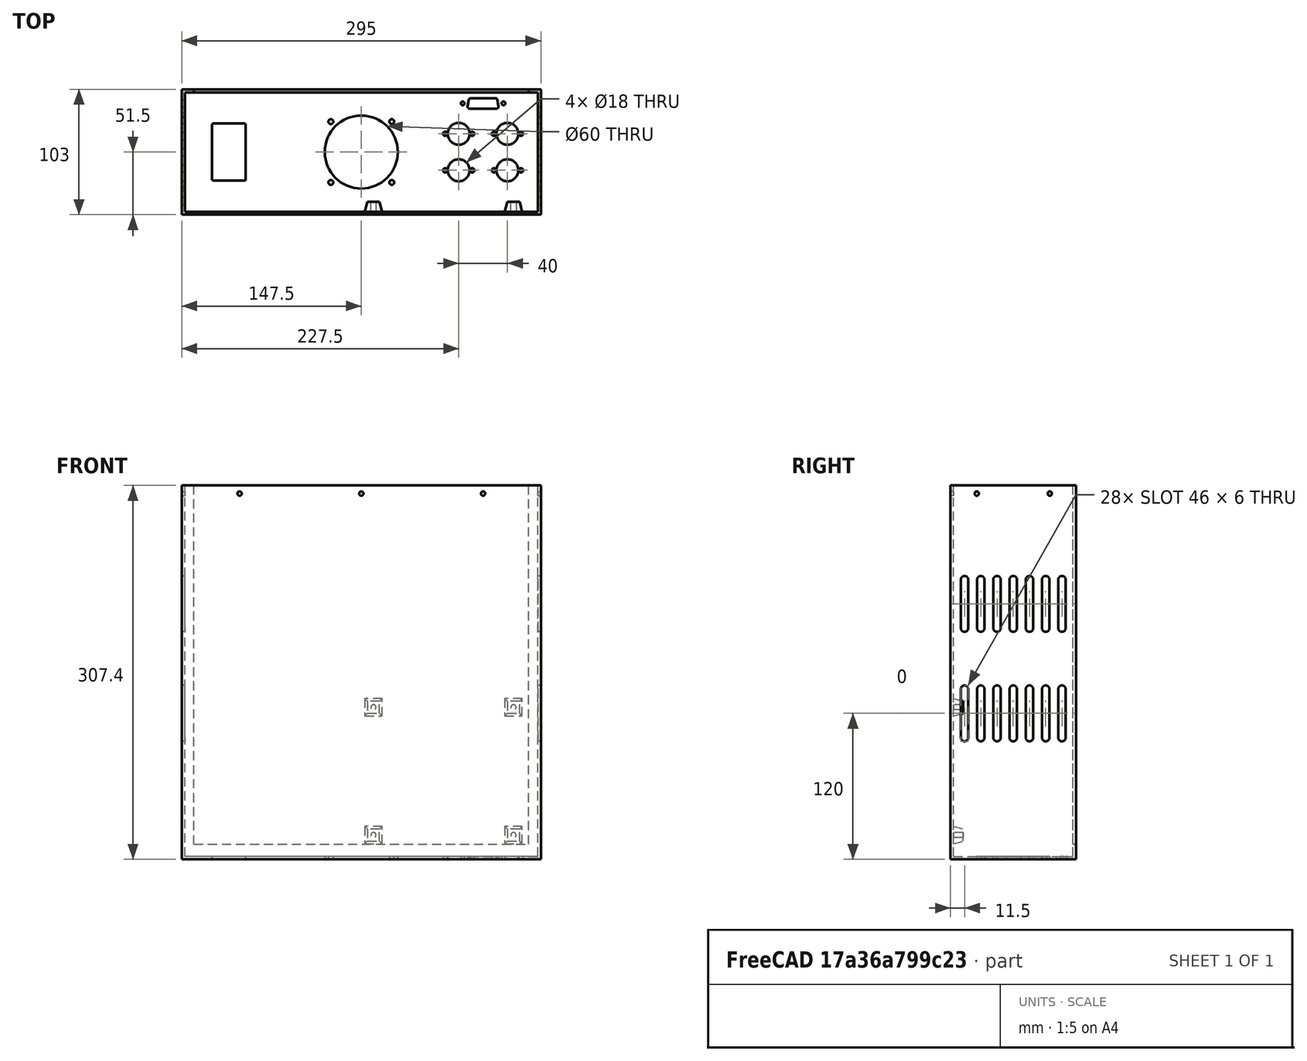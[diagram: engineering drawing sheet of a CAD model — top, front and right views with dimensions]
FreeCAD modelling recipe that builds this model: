
FCSTD DOCUMENT  (FreeCAD 1.0R39109 (Git))
Label: Main case
License: All rights reserved
LicenseURL: http://en.wikipedia.org/wiki/All_rights_reserved
objects: Sketcher::SketchObject×10, TechDraw::DrawViewDimension×7, PartDesign::Pocket×6, PartDesign::LinearPattern×6, PartDesign::Pad×4, PartDesign::MultiTransform×3, TechDraw::DrawSVGTemplate×2, TechDraw::DrawViewBalloon×2, TechDraw::DrawPage×2, PartDesign::Draft×1, PartDesign::Body×1, TechDraw::DrawProjGroupItem×1, TechDraw::DrawProjGroup×1, Mesh::Feature×1
note: 82 computed .brp shape members not serialized (recipe doc carries the construction recipe); baked Part::Feature solids carry a one-line shape summary decoded from their .brp

FEATURE [Sketcher::SketchObject] Sketch
  ArcFitTolerance = 0
  AttachmentSupport = -> [XY_Plane]
  FullyConstrained = true
  MakeInternals = false
  MapMode = 5
  sketch-geometry (4):
    g0: LineSegment StartX=-147.5 StartY=51.5 StartZ=0 EndX=147.5 EndY=51.5 EndZ=0
    g1: LineSegment StartX=147.5 StartY=51.5 StartZ=0 EndX=147.5 EndY=-51.5 EndZ=0
    g2: LineSegment StartX=147.5 StartY=-51.5 StartZ=0 EndX=-147.5 EndY=-51.5 EndZ=0
    g3: LineSegment StartX=-147.5 StartY=-51.5 StartZ=0 EndX=-147.5 EndY=51.5 EndZ=0
  constraints (11):
    c: Coincident(g0,g1)
    c: Coincident(g1,g2)
    c: Coincident(g2,g3)
    c: Coincident(g3,g0)
    c: Horizontal(g0)
    c: Horizontal(g2)
    c: Vertical(g1)
    c: Vertical(g3)
    c: Symmetric(g0,g1,g-1)
    c: DistanceX(g0,g0) = 295
    c: DistanceY(g1,g1) = 103
FEATURE [PartDesign::Pad] Pad  label="Rear panel"
  Direction = (0,0,1)
  Length = 2.4
  Length2 = 10
  Profile = -> Sketch
  ReferenceAxis = -> Sketch [N_Axis]
  Suppressed = false
  Type = 0
FEATURE [Sketcher::SketchObject] Sketch001
  ArcFitTolerance = 0
  AttachmentSupport = -> [Pad]
  FullyConstrained = true
  MakeInternals = false
  MapMode = 5
  Placement = pos=(0,0,2.4) rot=(0,0,1;0rad)
  sketch-geometry (14):
    g0: LineSegment [constr] StartX=-147.5 StartY=51.5 StartZ=0 EndX=147.5 EndY=51.5 EndZ=0
    g1: LineSegment StartX=147.5 StartY=51.5 StartZ=0 EndX=147.5 EndY=-51.5 EndZ=0
    g2: LineSegment StartX=147.5 StartY=-51.5 StartZ=0 EndX=-147.5 EndY=-51.5 EndZ=0
    g3: LineSegment StartX=-147.5 StartY=-51.5 StartZ=0 EndX=-147.5 EndY=51.5 EndZ=0
    g4: LineSegment [constr] StartX=-145 StartY=49 StartZ=0 EndX=145 EndY=49 EndZ=0
    g5: LineSegment StartX=145 StartY=49 StartZ=0 EndX=145 EndY=-49 EndZ=0
    g6: LineSegment StartX=145 StartY=-49 StartZ=0 EndX=-145 EndY=-49 EndZ=0
    g7: LineSegment StartX=-145 StartY=-49 StartZ=0 EndX=-145 EndY=49 EndZ=0
    g8: LineSegment StartX=-147.5 StartY=51.5 StartZ=0 EndX=-137.5 EndY=51.5 EndZ=0
    g9: LineSegment StartX=-137.5 StartY=51.5 StartZ=0 EndX=-137.5 EndY=49 EndZ=0
    g10: LineSegment StartX=-137.5 StartY=49 StartZ=0 EndX=-145 EndY=49 EndZ=0
    g11: LineSegment StartX=147.5 StartY=51.5 StartZ=0 EndX=137.5 EndY=51.5 EndZ=0
    g12: LineSegment StartX=137.5 StartY=51.5 StartZ=0 EndX=137.5 EndY=49 EndZ=0
    g13: LineSegment StartX=137.5 StartY=49 StartZ=0 EndX=145 EndY=49 EndZ=0
  constraints (38):
    c: Coincident(g0,g1)
    c: Coincident(g1,g2)
    c: Coincident(g2,g3)
    c: Coincident(g3,g0)
    c: Horizontal(g0)
    c: Horizontal(g2)
    c: Vertical(g1)
    c: Vertical(g3)
    c: Symmetric(g1,g0,g-1)
    c: DistanceX(g0,g0) = 295
    c: DistanceY(g3,g3) = 103
    c: Coincident(g4,g5)
    c: Coincident(g5,g6)
    c: Coincident(g6,g7)
    c: Coincident(g7,g4)
    c: Horizontal(g4)
    c: Horizontal(g6)
    c: Vertical(g5)
    c: Vertical(g7)
    c: Symmetric(g4,g5,g-1)
    c: DistanceX(g4,g4) = 290
    c: DistanceY(g7,g7) = 98
    c: Coincident(g3,g8)
    c: PointOnObject(g8,g0)
    c: Coincident(g8,g9)
    c: PointOnObject(g9,g4)
    c: Vertical(g9)
    c: Coincident(g9,g10)
    c: Coincident(g10,g7)
    c: DistanceX(g8,g8) = 10
    c: Coincident(g1,g11)
    c: PointOnObject(g11,g0)
    c: Coincident(g11,g12)
    c: PointOnObject(g12,g4)
    c: Coincident(g12,g13)
    c: Coincident(g13,g5)
    c: Vertical(g12)
    c: DistanceX(g11,g11) = 10
FEATURE [PartDesign::Pad] Pad001  label="Bottom and sides"
  BaseFeature = -> Pad
  Direction = (0,0,1)
  Length = 305
  Length2 = 10
  Profile = -> Sketch001
  ReferenceAxis = -> Sketch001 [N_Axis]
  Suppressed = false
  Type = 0
FEATURE [Sketcher::SketchObject] Sketch002
  ArcFitTolerance = 0
  AttachmentSupport = -> [Pad001]
  FullyConstrained = true
  MakeInternals = false
  MapMode = 5
  Placement = pos=(0,0,2.4) rot=(0,0,1;0rad)
  sketch-geometry (4):
    g0: LineSegment StartX=-137.5 StartY=51.5 StartZ=0 EndX=137.5 EndY=51.5 EndZ=0
    g1: LineSegment StartX=137.5 StartY=51.5 StartZ=0 EndX=137.5 EndY=49 EndZ=0
    g2: LineSegment StartX=137.5 StartY=49 StartZ=0 EndX=-137.5 EndY=49 EndZ=0
    g3: LineSegment StartX=-137.5 StartY=49 StartZ=0 EndX=-137.5 EndY=51.5 EndZ=0
  constraints (11):
    c: Coincident(g0,g1)
    c: Coincident(g1,g2)
    c: Coincident(g2,g3)
    c: Coincident(g3,g0)
    c: Horizontal(g0)
    c: Vertical(g1)
    c: Vertical(g3)
    c: DistanceX(g0,g0) = 275
    c: DistanceY(g-1,g0) = 51.5
    c: DistanceY(g3,g3) = 2.5
    c: Symmetric(g1,g2,g-2)
FEATURE [PartDesign::Pad] Pad002  label="Rear top return"
  BaseFeature = -> Pad001
  Direction = (0,0,1)
  Length = 10
  Length2 = 10
  Profile = -> Sketch002
  ReferenceAxis = -> Sketch002 [N_Axis]
  Suppressed = false
  Type = 0
FEATURE [Sketcher::SketchObject] Sketch003
  ArcFitTolerance = 0
  AttachmentSupport = -> [Pad002]
  FullyConstrained = true
  MakeInternals = false
  MapMode = 5
  Placement = pos=(-147.5,0,0) rot=(0.57735,-0.57735,-0.57735;2.0944rad)
  sketch-geometry (4):
    g0: ArcOfCircle CenterX=40 CenterY=140 CenterZ=0 NormalX=0 NormalY=0 NormalZ=1 AngleXU=0 Radius=3 StartAngle=-2.7e-15 EndAngle=3.14159
    g1: ArcOfCircle CenterX=40 CenterY=100 CenterZ=0 NormalX=0 NormalY=0 NormalZ=1 AngleXU=0 Radius=3 StartAngle=3.14159 EndAngle=6.28319
    g2: LineSegment StartX=37 StartY=140 StartZ=0 EndX=37 EndY=100 EndZ=0
    g3: LineSegment StartX=43 StartY=100 StartZ=0 EndX=43 EndY=140 EndZ=0
  constraints (10):
    c: Tangent(g0,g2) = -1.5708
    c: Tangent(g2,g1) = -1.5708
    c: Tangent(g1,g3) = -1.5708
    c: Tangent(g3,g0) = -1.5708
    c: Equal(g0,g1)
    c: Vertical(g2)
    c: Diameter(g1) = 6
    c: DistanceY(g1,g0) = 40
    c: DistanceY(g-1,g1) = 100
    c: DistanceX(g-1,g1) = 40
FEATURE [PartDesign::Pocket] Pocket  label="Vent hole"
  BaseFeature = -> Pad002
  Direction = (1,0,0)
  Length = 5
  Length2 = 5
  Profile = -> Sketch003
  ReferenceAxis = -> Sketch003 [N_Axis]
  Suppressed = false
  Type = 1
FEATURE [PartDesign::LinearPattern] LinearPattern
  Direction = -> Sketch003 [V_Axis]
  Length = 90
  Mode = 0
  Occurrences = 2
  Offset = 90
  Suppressed = false
  TransformMode = 0
FEATURE [PartDesign::LinearPattern] LinearPattern001
  Direction = -> Sketch003 [H_Axis]
  Length = 80
  Mode = 0
  Occurrences = 7
  Offset = 13.3333
  Reversed = true
  Suppressed = false
  TransformMode = 0
FEATURE [PartDesign::MultiTransform] MultiTransform  label="Vent hole array"
  BaseFeature = -> Pocket
  Originals = -> [Pocket]
  Suppressed = false
  TransformMode = 0
  Transformations = -> [LinearPattern,LinearPattern001]
FEATURE [Sketcher::SketchObject] Sketch004
  ArcFitTolerance = 0
  AttachmentSupport = -> [MultiTransform]
  FullyConstrained = true
  MakeInternals = false
  MapMode = 5
  Placement = pos=(0,0,0) rot=(1,0,0;3.14159rad)
  sketch-geometry (19):
    g0: ArcOfCircle CenterX=-121.5 CenterY=22.5 CenterZ=0 NormalX=0 NormalY=0 NormalZ=1 AngleXU=0 Radius=1 StartAngle=1.5708 EndAngle=3.14159
    g1: LineSegment StartX=-121.5 StartY=23.5 StartZ=0 EndX=-96 EndY=23.5 EndZ=0
    g2: ArcOfCircle CenterX=-96 CenterY=22.5 CenterZ=0 NormalX=0 NormalY=0 NormalZ=1 AngleXU=0 Radius=1 StartAngle=8e-16 EndAngle=1.5708
    g3: LineSegment StartX=-95 StartY=22.5 StartZ=0 EndX=-95 EndY=-22.5 EndZ=0
    g4: ArcOfCircle CenterX=-96 CenterY=-22.5 CenterZ=0 NormalX=0 NormalY=0 NormalZ=1 AngleXU=0 Radius=1 StartAngle=4.71239 EndAngle=6.28319
    g5: LineSegment StartX=-96 StartY=-23.5 StartZ=0 EndX=-121.5 EndY=-23.5 EndZ=0
    g6: ArcOfCircle CenterX=-121.5 CenterY=-22.5 CenterZ=0 NormalX=0 NormalY=0 NormalZ=1 AngleXU=0 Radius=1 StartAngle=3.14159 EndAngle=4.71239
    g7: LineSegment StartX=-122.5 StartY=-22.5 StartZ=0 EndX=-122.5 EndY=22.5 EndZ=0
    g8: GeomPoint [constr] X=-122.5 Y=23.5 Z=0
    g9: GeomPoint [constr] X=-95 Y=-23.5 Z=0
    g10: Circle CenterX=0 CenterY=0 CenterZ=0 NormalX=0 NormalY=0 NormalZ=1 AngleXU=0 Radius=30
    g11: Circle CenterX=-25 CenterY=25 CenterZ=0 NormalX=0 NormalY=0 NormalZ=1 AngleXU=0 Radius=2
    g12: Circle CenterX=25 CenterY=25 CenterZ=0 NormalX=0 NormalY=0 NormalZ=1 AngleXU=0 Radius=2
    g13: Circle CenterX=-25 CenterY=-25 CenterZ=0 NormalX=0 NormalY=0 NormalZ=1 AngleXU=0 Radius=2
    g14: Circle CenterX=25 CenterY=-25 CenterZ=0 NormalX=0 NormalY=0 NormalZ=1 AngleXU=0 Radius=2
    g15: LineSegment [constr] StartX=-25 StartY=25 StartZ=0 EndX=25 EndY=25 EndZ=0
    g16: LineSegment [constr] StartX=25 StartY=25 StartZ=0 EndX=25 EndY=-25 EndZ=0
    g17: LineSegment [constr] StartX=25 StartY=-25 StartZ=0 EndX=-25 EndY=-25 EndZ=0
    g18: LineSegment [constr] StartX=-25 StartY=-25 StartZ=0 EndX=-25 EndY=25 EndZ=0
  constraints (44):
    c: Tangent(g0,g1) = 1.5708
    c: Tangent(g1,g2) = 1.5708
    c: Tangent(g2,g3) = 1.5708
    c: Tangent(g3,g4) = 1.5708
    c: Tangent(g4,g5) = 1.5708
    c: Tangent(g5,g6) = 1.5708
    c: Tangent(g6,g7) = 1.5708
    c: Tangent(g7,g0) = 1.5708
    c: Horizontal(g1)
    c: Horizontal(g5)
    c: Vertical(g3)
    c: Vertical(g7)
    c: Equal(g0,g2)
    c: Equal(g4,g6)
    c: PointOnObject(g8,g1)
    c: PointOnObject(g8,g7)
    c: PointOnObject(g9,g3)
    c: PointOnObject(g9,g5)
    c: Symmetric(g2,g4,g-1)
    c: Diameter(g0) = 2
    c: Coincident(g10,g-1)
    c: DistanceX(g0,g2) = 27.5
    c: DistanceY(g4,g1) = 47
    c: DistanceX(g2,g10) = 95
    c: Diameter(g10) = 60
    c: Coincident(g15,g16)
    c: Coincident(g16,g17)
    c: Coincident(g17,g18)
    c: Coincident(g18,g15)
    c: Horizontal(g15)
    c: Horizontal(g17)
    c: Vertical(g16)
    c: Vertical(g18)
    c: Coincident(g15,g11)
    c: Coincident(g16,g14)
    c: Symmetric(g14,g11,g10)
    c: Coincident(g12,g15)
    c: Coincident(g13,g17)
    c: Equal(g15,g18)
    c: DistanceX(g15,g15) = 50
    c: Equal(g11,g13)
    c: Equal(g11,g14)
    c: Equal(g11,g12)
    c: Diameter(g11) = 4
FEATURE [PartDesign::Pocket] Pocket001  label="Fan hole"
  BaseFeature = -> MultiTransform
  Direction = (0,0,1)
  Length = 5
  Length2 = 5
  Profile = -> Sketch004
  ReferenceAxis = -> Sketch004 [N_Axis]
  Suppressed = false
  Type = 0
FEATURE [Sketcher::SketchObject] Sketch005
  ArcFitTolerance = 0
  AttachmentSupport = -> [Pocket001]
  FullyConstrained = true
  MakeInternals = false
  MapMode = 5
  Placement = pos=(0,0,0) rot=(1,0,0;3.14159rad)
  sketch-geometry (3):
    g0: Circle CenterX=80 CenterY=-15 CenterZ=0 NormalX=0 NormalY=0 NormalZ=1 AngleXU=0 Radius=9
    g1: Circle CenterX=68.9 CenterY=-15 CenterZ=0 NormalX=0 NormalY=0 NormalZ=1 AngleXU=0 Radius=1.75
    g2: Circle CenterX=91.1 CenterY=-15 CenterZ=0 NormalX=0 NormalY=0 NormalZ=1 AngleXU=0 Radius=1.75
  constraints (8):
    c: DistanceY(g0,g-1) = 15
    c: DistanceX(g-1,g0) = 80
    c: Diameter(g0) = 18
    c: Symmetric(g2,g1,g0)
    c: Equal(g1,g2)
    c: Diameter(g1) = 3.5
    c: DistanceX(g1,g2) = 22.2
    c: Horizontal(g1,g2)
FEATURE [PartDesign::Pocket] Pocket002  label="Din Holes"
  BaseFeature = -> Pocket001
  Direction = (0,0,1)
  Length = 5
  Length2 = 5
  Profile = -> Sketch005
  ReferenceAxis = -> Sketch005 [N_Axis]
  Suppressed = false
  Type = 0
FEATURE [PartDesign::LinearPattern] LinearPattern002
  Direction = -> Sketch005 [H_Axis]
  Length = 40
  Mode = 0
  Occurrences = 2
  Offset = 40
  Suppressed = false
  TransformMode = 0
FEATURE [PartDesign::LinearPattern] LinearPattern003
  Direction = -> Sketch005 [V_Axis]
  Length = 30
  Mode = 0
  Occurrences = 2
  Offset = 30
  Suppressed = false
  TransformMode = 0
FEATURE [PartDesign::MultiTransform] MultiTransform001  label="Din hole 2 x 2 array"
  BaseFeature = -> Pocket002
  Originals = -> [Pocket002]
  Suppressed = false
  TransformMode = 0
  Transformations = -> [LinearPattern002,LinearPattern003]
FEATURE [Sketcher::SketchObject] Sketch006
  ArcFitTolerance = 0
  AttachmentSupport = -> [MultiTransform001]
  ExternalGeometry = -> [MultiTransform001]
  FullyConstrained = true
  MakeInternals = false
  MapMode = 5
  Placement = pos=(0,0,0) rot=(1,0,0;3.14159rad)
  sketch-geometry (15):
    g0: LineSegment StartX=87.315 StartY=-37.5105 StartZ=0 EndX=88.2848 EndY=-43.0105 EndZ=0
    g1: LineSegment StartX=89.762 StartY=-44.25 StartZ=0 EndX=110.238 EndY=-44.25 EndZ=0
    g2: LineSegment StartX=111.715 StartY=-43.0105 StartZ=0 EndX=112.685 EndY=-37.5105 EndZ=0
    g3: LineSegment StartX=111.208 StartY=-35.75 StartZ=0 EndX=88.7922 EndY=-35.75 EndZ=0
    g4: ArcOfCircle CenterX=89.762 CenterY=-42.75 CenterZ=0 NormalX=0 NormalY=0 NormalZ=1 AngleXU=0 Radius=1.5 StartAngle=3.31613 EndAngle=4.71239
    g5: ArcOfCircle CenterX=111.208 CenterY=-37.25 CenterZ=0 NormalX=0 NormalY=0 NormalZ=1 AngleXU=0 Radius=1.5 StartAngle=6.10865 EndAngle=7.85398
    g6: ArcOfCircle CenterX=110.238 CenterY=-42.75 CenterZ=0 NormalX=0 NormalY=0 NormalZ=1 AngleXU=0 Radius=1.5 StartAngle=4.71239 EndAngle=6.10865
    g7: ArcOfCircle CenterX=88.7922 CenterY=-37.25 CenterZ=0 NormalX=0 NormalY=0 NormalZ=1 AngleXU=0 Radius=1.5 StartAngle=1.5708 EndAngle=3.31613
    g8: LineSegment [constr] StartX=83.25 StartY=-40 StartZ=0 EndX=116.75 EndY=-40 EndZ=0
    g9: GeomPoint [constr] X=100 Y=-35.75 Z=0
    g10: LineSegment [constr] StartX=100 StartY=-35.75 StartZ=0 EndX=100 EndY=-44.25 EndZ=0
    g11: Circle CenterX=83.25 CenterY=-40 CenterZ=0 NormalX=0 NormalY=0 NormalZ=1 AngleXU=0 Radius=1.5
    g12: Circle CenterX=116.75 CenterY=-40 CenterZ=0 NormalX=0 NormalY=0 NormalZ=1 AngleXU=0 Radius=1.5
    g13: LineSegment [constr] StartX=100 StartY=-44.25 StartZ=0 EndX=100 EndY=15 EndZ=0
    g14: LineSegment [constr] StartX=80 StartY=15 StartZ=0 EndX=120 EndY=15 EndZ=0
  constraints (35):
    c: Horizontal(g1)
    c: Horizontal(g3)
    c: Equal(g2,g0)
    c: Tangent(g0,g4) = -1.5708
    c: Tangent(g1,g4) = -1.5708
    c: Tangent(g3,g5) = -1.5708
    c: Tangent(g2,g5) = -1.5708
    c: Tangent(g1,g6) = -1.5708
    c: Tangent(g2,g6) = -1.5708
    c: Tangent(g3,g7) = -1.5708
    c: Tangent(g0,g7) = -1.5708
    c: Equal(g5,g7)
    c: Equal(g7,g4)
    c: Equal(g4,g6)
    c: Diameter(g7) = 3
    c: DistanceX(g0,g2) = 25.37
    c: Angle(g0,g3) = 1.39626
    c: DistanceY(g1,g3) = 8.5
    c: Horizontal(g8)
    c: Distance(g3,g8) = 4.25
    c: Symmetric(g3,g3,g9)
    c: Coincident(g10,g9)
    c: PointOnObject(g10,g1)
    c: Coincident(g11,g8)
    c: Coincident(g12,g8)
    c: Equal(g11,g12)
    c: Diameter(g11) = 3
    c: DistanceX(g11,g12) = 33.5
    c: Symmetric(g11,g12,g10)
    c: Coincident(g13,g10)
    c: Vertical(g13)
    c: Coincident(g14,g-3)
    c: Coincident(g14,g-4)
    c: Symmetric(g14,g14,g13)
    c: DistanceY(g11,g-5) = 25
FEATURE [PartDesign::Pocket] Pocket003  label="DB15 hole"
  BaseFeature = -> MultiTransform001
  Direction = (0,0,1)
  Length = 5
  Length2 = 5
  Profile = -> Sketch006
  ReferenceAxis = -> Sketch006 [N_Axis]
  Suppressed = false
  Type = 0
FEATURE [Sketcher::SketchObject] Sketch007
  ArcFitTolerance = 0
  AttachmentSupport = -> [Pocket003]
  FullyConstrained = true
  MakeInternals = false
  MapMode = 5
  Placement = pos=(0,-49,0) rot=(0,0.707107,0.707107;3.14159rad)
  sketch-geometry (5):
    g0: LineSegment StartX=-130 StartY=25 StartZ=0 EndX=-120 EndY=25 EndZ=0
    g1: LineSegment StartX=-120 StartY=25 StartZ=0 EndX=-120 EndY=15 EndZ=0
    g2: LineSegment StartX=-120 StartY=15 StartZ=0 EndX=-130 EndY=15 EndZ=0
    g3: LineSegment StartX=-130 StartY=15 StartZ=0 EndX=-130 EndY=25 EndZ=0
    g4: Circle CenterX=-125 CenterY=20 CenterZ=0 NormalX=0 NormalY=0 NormalZ=1 AngleXU=0 Radius=2.1
  constraints (14):
    c: Coincident(g0,g1)
    c: Coincident(g1,g2)
    c: Coincident(g2,g3)
    c: Coincident(g3,g0)
    c: Horizontal(g0)
    c: Horizontal(g2)
    c: Vertical(g1)
    c: Vertical(g3)
    c: DistanceX(g0,g0) = 10
    c: Equal(g0,g3)
    c: Symmetric(g2,g0,g4)
    c: Diameter(g4) = 4.2
    c: DistanceY(g-1,g4) = 20
    c: DistanceX(g4,g-1) = 125
FEATURE [PartDesign::Pad] Pad003  label="PSU Standoff "
  BaseFeature = -> Pocket003
  Direction = (0,1,-2e-16)
  Length = 8
  Length2 = 10
  Profile = -> Sketch007
  ReferenceAxis = -> Sketch007 [N_Axis]
  Suppressed = false
  Type = 0
FEATURE [PartDesign::Draft] Draft  label="PSU standotff Draft"
  Angle = 15
  Base = -> Pad003 [Face170,Face171,Face173,Face172]
  BaseFeature = -> Pad003
  NeutralPlane = -> Pad003 [Face174]
  SupportTransform = false
  Suppressed = false
FEATURE [PartDesign::LinearPattern] LinearPattern004
  Direction = -> Sketch007 [H_Axis]
  Length = 115
  Mode = 0
  Occurrences = 2
  Offset = 115
  Suppressed = false
  TransformMode = 0
FEATURE [PartDesign::LinearPattern] LinearPattern005
  Direction = -> Sketch007 [V_Axis]
  Length = 105
  Mode = 0
  Occurrences = 2
  Offset = 105
  Suppressed = false
  TransformMode = 0
FEATURE [PartDesign::MultiTransform] MultiTransform002  label="PSU standoff array"
  BaseFeature = -> Draft
  Originals = -> [Pad003,Draft]
  Suppressed = false
  TransformMode = 0
  Transformations = -> [LinearPattern004,LinearPattern005]
FEATURE [Sketcher::SketchObject] Sketch008
  ArcFitTolerance = 0
  AttachmentSupport = -> [MultiTransform002]
  ExternalGeometry = -> [MultiTransform002]
  FullyConstrained = true
  MakeInternals = false
  MapMode = 5
  Placement = pos=(147.5,0,0) rot=(0.57735,0.57735,0.57735;2.0944rad)
  sketch-geometry (2):
    g0: Circle CenterX=-30 CenterY=300.7 CenterZ=0 NormalX=0 NormalY=0 NormalZ=1 AngleXU=0 Radius=1.75
    g1: Circle CenterX=30 CenterY=300.7 CenterZ=0 NormalX=0 NormalY=0 NormalZ=1 AngleXU=0 Radius=1.75
  constraints (5):
    c: Equal(g0,g1)
    c: Diameter(g0) = 3.5
    c: DistanceX(g0,g1) = 60
    c: Symmetric(g0,g1,g-2)
    c: DistanceY(g0,g-3) = 6.7
FEATURE [PartDesign::Pocket] Pocket004  label="Front side comp mounting hole"
  BaseFeature = -> MultiTransform002
  Direction = (-1,0,0)
  Length = 5
  Length2 = 5
  Profile = -> Sketch008
  ReferenceAxis = -> Sketch008 [N_Axis]
  Suppressed = false
  Type = 1
FEATURE [Sketcher::SketchObject] Sketch009
  ArcFitTolerance = 0
  AttachmentSupport = -> [Pocket004]
  ExternalGeometry = -> [Pocket004]
  FullyConstrained = true
  MakeInternals = false
  MapMode = 5
  Placement = pos=(0,-51.5,0) rot=(1,0,0;1.5708rad)
  sketch-geometry (3):
    g0: Circle CenterX=-100 CenterY=300.7 CenterZ=0 NormalX=0 NormalY=0 NormalZ=1 AngleXU=0 Radius=1.75
    g1: Circle CenterX=0 CenterY=300.7 CenterZ=0 NormalX=0 NormalY=0 NormalZ=1 AngleXU=0 Radius=1.75
    g2: Circle CenterX=100 CenterY=300.7 CenterZ=0 NormalX=0 NormalY=0 NormalZ=1 AngleXU=0 Radius=1.75
  constraints (8):
    c: PointOnObject(g1,g-2)
    c: Symmetric(g2,g0,g1)
    c: Equal(g0,g1)
    c: Equal(g0,g2)
    c: Diameter(g0) = 3.5
    c: DistanceX(g0,g2) = 200
    c: DistanceY(g1,g-3) = 6.7
    c: Horizontal(g2,g0)
FEATURE [PartDesign::Pocket] Pocket005  label="Front bottom mounting holes"
  BaseFeature = -> Pocket004
  Direction = (0,1,-2e-16)
  Length = 5
  Length2 = 5
  Profile = -> Sketch009
  ReferenceAxis = -> Sketch009 [N_Axis]
  Suppressed = false
  Type = 0
FEATURE [PartDesign::Body] Body
  AllowCompound = false
  Group = -> [Sketch,Pad,Sketch001,Pad001,Sketch002,Pad002,Sketch003,Pocket,MultiTransform,LinearPattern,LinearPattern001,Sketch004,Pocket001,Sketch005,Pocket002,MultiTransform001,LinearPattern002,LinearPattern003,Sketch006,Pocket003,Sketch007,Pad003,Draft,MultiTransform002,LinearPattern004,LinearPattern005,Sketch008,Pocket004,Sketch009,Pocket005]
  Origin = -> Origin
  Tip = -> Pocket005
FEATURE [TechDraw::DrawSVGTemplate] Template
  EditableTexts = APPROVER_NAME=APPROVER NAME; AUTHOR_NAME=AUTHOR NAME; DATE=YYYY-MM-DD; DN=DN; DOCUMENT_TYPE=Mechanical assembly drawing; OWNER_NAME=OWNER NAME; PM=PM; PN=PN; REVISION=REV A; RIGHTS=(R) DO NOT DUPLICATE THIS DRAWING TO THIRD PARTIES WITHOUT OWNER'S PERMISSION!; SCALE=M x:x; SHEET=99 of 99; SIZE=A3; TITLELINE-1=FreeCAD; TOLERANCE=+/- ?
  Height = 297
  Orientation = 1
  Template = /Applications/FreeCAD.app/Contents/Resources/share/Mod/TechDraw/Templates/A3_Landscape_ISO7200_Pep.svg
  Width = 420
FEATURE [TechDraw::DrawProjGroupItem] ProjItem  label="Front"
  CoarseView = false
  Direction = (0,0,1)
  Focus = 100
  HardHidden = false
  IsoCount = 0
  IsoHidden = false
  IsoVisible = false
  LockPosition = true
  Perspective = false
  Rotation = 0
  RotationVector = (1,0,0)
  ScaleType = 2
  ScrubCount = 0
  SeamHidden = false
  SeamVisible = true
  SmoothHidden = false
  SmoothVisible = true
  Source = -> [Body]
  Type = 0
  X = 0
  XDirection = (1,0,0)
  Y = 0
FEATURE [TechDraw::DrawProjGroup] ProjGroup
  Anchor = -> ProjItem
  AutoDistribute = true
  LockPosition = false
  ProjectionType = 0
  Rotation = 0
  ScaleType = 0
  Source = -> [Body]
  Views = -> [ProjItem]
  X = 210
  Y = 148.5
  spacingX = 15
  spacingY = 15
FEATURE [TechDraw::DrawViewDimension] Dimension
  AngleOverride = false
  Arbitrary = false
  ArbitraryTolerances = false
  EqualTolerance = true
  ExtensionAngle = 0
  FormatSpec = %.3f
  FormatSpecOverTolerance = %+.3f
  FormatSpecUnderTolerance = %+.3f
  Inverted = false
  LineAngle = 0
  LockPosition = false
  MeasureType = 1
  OverTolerance = 0
  References2D = -> [ProjItem]
  Rotation = 0
  ScaleType = 0
  TheoreticalExact = false
  Type = 1
  UnderTolerance = 0
  X = 1.18977
  Y = -73.2698
FEATURE [TechDraw::DrawViewDimension] Dimension001
  AngleOverride = false
  Arbitrary = false
  ArbitraryTolerances = false
  EqualTolerance = true
  ExtensionAngle = 0
  FormatSpec = %.3f
  FormatSpecOverTolerance = %+.3f
  FormatSpecUnderTolerance = %+.3f
  Inverted = false
  LineAngle = 0
  LockPosition = false
  MeasureType = 1
  OverTolerance = 0
  References2D = -> [ProjItem]
  Rotation = 0
  ScaleType = 0
  TheoreticalExact = false
  Type = 1
  UnderTolerance = 0
  X = 1.18977
  Y = -83.7016
FEATURE [TechDraw::DrawViewDimension] Dimension002
  AngleOverride = false
  Arbitrary = false
  ArbitraryTolerances = false
  EqualTolerance = true
  ExtensionAngle = 0
  FormatSpec = %.3f
  FormatSpecOverTolerance = %+.3f
  FormatSpecUnderTolerance = %+.3f
  Inverted = false
  LineAngle = 0
  LockPosition = false
  MeasureType = 1
  OverTolerance = 0
  References2D = -> [ProjItem]
  Rotation = 0
  ScaleType = 0
  TheoreticalExact = false
  Type = 2
  UnderTolerance = 0
  X = 174.27
  Y = 3.09489
FEATURE [TechDraw::DrawViewDimension] Dimension003
  AngleOverride = false
  Arbitrary = false
  ArbitraryTolerances = false
  EqualTolerance = true
  ExtensionAngle = 0
  FormatSpec = %.3f
  FormatSpecOverTolerance = %+.3f
  FormatSpecUnderTolerance = %+.3f
  Inverted = false
  LineAngle = 0
  LockPosition = false
  MeasureType = 1
  OverTolerance = 0
  References2D = -> [ProjItem]
  Rotation = 0
  ScaleType = 0
  TheoreticalExact = false
  Type = 2
  UnderTolerance = 0
  X = 161.26
  Y = 2.30171
FEATURE [TechDraw::DrawViewDimension] Dimension004
  AngleOverride = false
  Arbitrary = false
  ArbitraryTolerances = false
  EqualTolerance = true
  ExtensionAngle = 0
  FormatSpec = %.3f
  FormatSpecOverTolerance = %+.3f
  FormatSpecUnderTolerance = %+.3f
  Inverted = false
  LineAngle = 0
  LockPosition = false
  MeasureType = 1
  OverTolerance = 0
  References2D = -> [ProjItem]
  Rotation = 0
  ScaleType = 0
  TheoreticalExact = false
  Type = 1
  UnderTolerance = 0
  X = -109.236
  Y = 41.5373
FEATURE [TechDraw::DrawViewDimension] Dimension005
  AngleOverride = false
  Arbitrary = false
  ArbitraryTolerances = false
  EqualTolerance = true
  ExtensionAngle = 0
  FormatSpec = %.3f
  FormatSpecOverTolerance = %+.3f
  FormatSpecUnderTolerance = %+.3f
  Inverted = false
  LineAngle = 0
  LockPosition = false
  MeasureType = 1
  OverTolerance = 0
  References2D = -> [ProjItem]
  Rotation = 0
  ScaleType = 0
  TheoreticalExact = false
  Type = 2
  UnderTolerance = 0
  X = -83.6781
  Y = 3.95917
FEATURE [TechDraw::DrawViewBalloon] Balloon
  BubbleShape = 6
  EndType = 0
  EndTypeScale = 1
  KinkLength = 5
  LockPosition = false
  OriginX = -122.5
  OriginY = 0
  Rotation = 0
  ScaleType = 0
  ShapeScale = 1
  SourceView = -> ProjItem
  Text = 1|IEC
  TextWrapLen = -1
  X = -136.385
  Y = 9.62367
FEATURE [TechDraw::DrawViewBalloon] Balloon001
  BubbleShape = 6
  EndType = 0
  EndTypeScale = 1
  KinkLength = 5
  LockPosition = false
  OriginX = 72.5
  OriginY = 15
  Rotation = 0
  ScaleType = 0
  ShapeScale = 1
  SourceView = -> ProjItem
  Text = 3|6 Pin DIN
  TextWrapLen = -1
  X = 46.2929
  Y = 29.974
FEATURE [TechDraw::DrawViewDimension] Dimension006
  AngleOverride = false
  Arbitrary = false
  ArbitraryTolerances = false
  EqualTolerance = true
  ExtensionAngle = 0
  FormatSpec = %.3f
  FormatSpecOverTolerance = %+.3f
  FormatSpecUnderTolerance = %+.3f
  Inverted = false
  LineAngle = 0
  LockPosition = false
  MeasureType = 1
  OverTolerance = 0
  References2D = -> [ProjItem]
  Rotation = 0
  ScaleType = 0
  TheoreticalExact = false
  Type = 1
  UnderTolerance = 0
  X = -0.972781
  Y = 68.7539
FEATURE [TechDraw::DrawPage] Page
  KeepUpdated = true
  NextBalloonIndex = 4
  ProjectionType = 0
  Template = -> Template
  Views = -> [ProjGroup,Dimension,Dimension001,Dimension002,Dimension003,Dimension004,Dimension005,Balloon,Balloon001,Dimension006]
FEATURE [TechDraw::DrawSVGTemplate] Template001
  EditableTexts = Designed_by_Name=Designed by Name; Drawing_number=Drawing number; FC-Date=Date; FC-SC=Scale; FC-SH=Sheet; FC-Title=Title; Subtitle=Subtitle; Weight=Weight
  Height = 210
  Orientation = 1
  Template = /Applications/FreeCAD.app/Contents/Resources/share/Mod/TechDraw/Templates/A4_LandscapeTD.svg
  Width = 297
FEATURE [TechDraw::DrawPage] Page001
  KeepUpdated = true
  NextBalloonIndex = 1
  ProjectionType = 0
  Template = -> Template001
FEATURE [Mesh::Feature] Mesh  label="Body (Meshed)"
